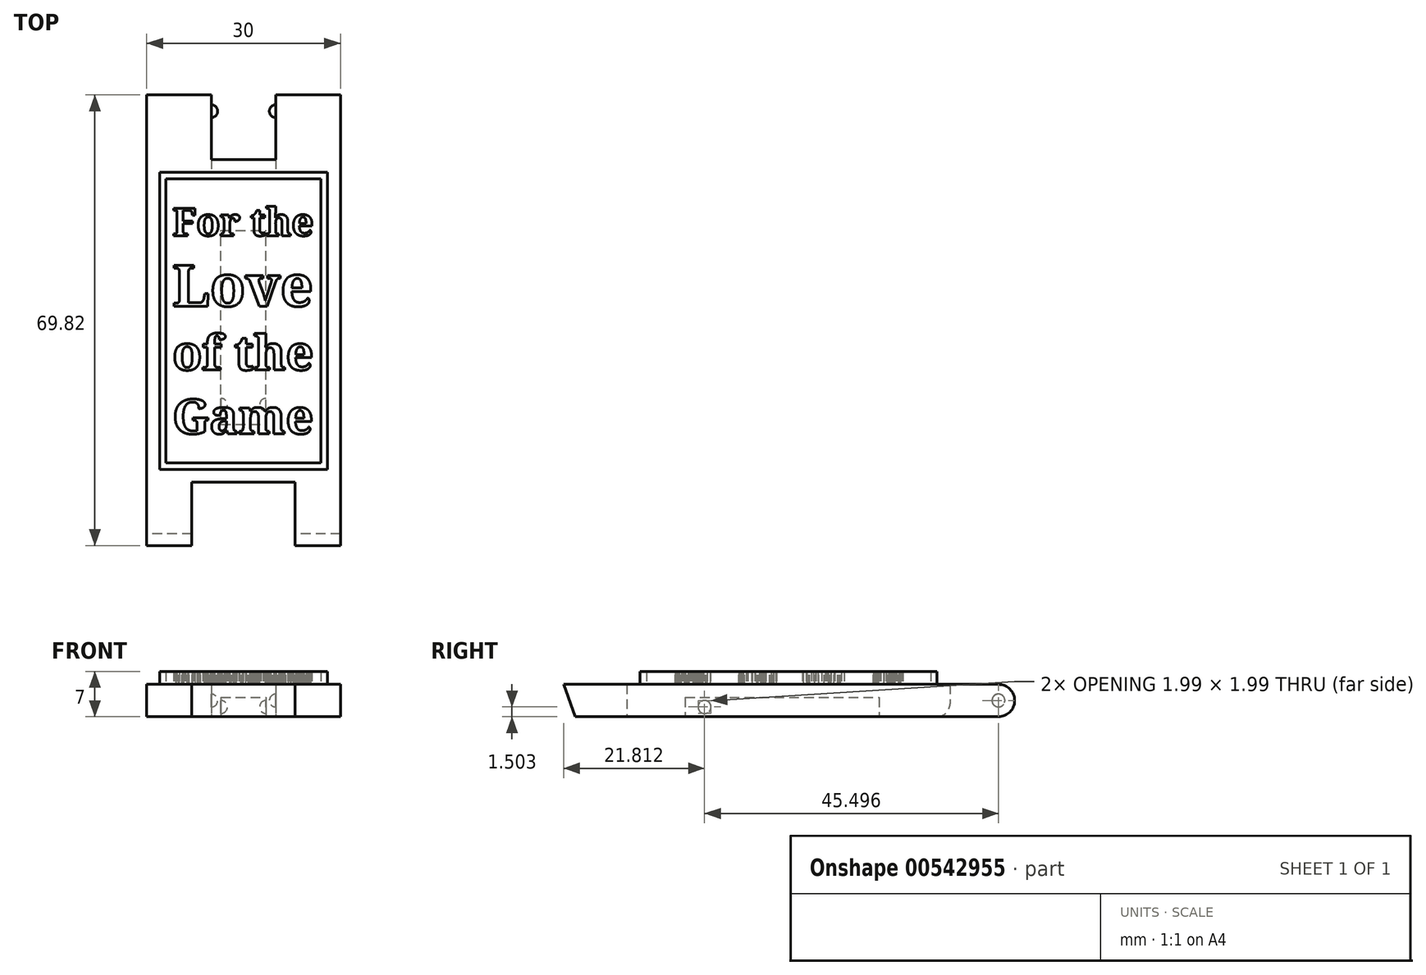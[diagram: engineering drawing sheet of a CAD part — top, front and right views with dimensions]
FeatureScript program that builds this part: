
annotation { "Feature Type Name" : "Feature", "Feature Type Description" : "" }
export const myFeature = defineFeature(function(context is Context, id is Id, definition is map)
    precondition{}
    {
        {
            var Q0;
            Q0=qCreatedBy(makeId("Top.planeOp"),FACE);
            var sketch = newSketch(context, id + "F0", { "sketchPlane" : qUnion([Q0])});
            skLineSegment(sketch, "E0.bottom", {"start": v(-23.2, 19.17) * mm, "end": v(6.8, 19.17) * mm});
            skLineSegment(sketch, "E0.top", {"start": v(-23.2, -30.83) * mm, "end": v(6.8, -30.83) * mm});
            skLineSegment(sketch, "E0.left", {"start": v(-23.2, 19.17) * mm, "end": v(-23.2, -30.83) * mm});
            skLineSegment(sketch, "E0.right", {"start": v(6.8, 19.17) * mm, "end": v(6.8, -30.83) * mm});
            skLineSegment(sketch, "E1.bottom", {"start": v(-23.2, 19.17) * mm, "end": v(-13.2, 19.17) * mm});
            skLineSegment(sketch, "E1.top", {"start": v(-23.2, 29.17) * mm, "end": v(-13.2, 29.17) * mm});
            skLineSegment(sketch, "E1.left", {"start": v(-23.2, 19.17) * mm, "end": v(-23.2, 29.17) * mm});
            skLineSegment(sketch, "E1.right", {"start": v(-13.2, 19.17) * mm, "end": v(-13.2, 29.17) * mm});
            skLineSegment(sketch, "E2.bottom", {"start": v(6.8, 19.17) * mm, "end": v(-3.2, 19.17) * mm});
            skLineSegment(sketch, "E2.top", {"start": v(6.8, 29.17) * mm, "end": v(-3.2, 29.17) * mm});
            skLineSegment(sketch, "E2.left", {"start": v(6.8, 19.17) * mm, "end": v(6.8, 29.17) * mm});
            skLineSegment(sketch, "E2.right", {"start": v(-3.2, 19.17) * mm, "end": v(-3.2, 29.17) * mm});
            skLineSegment(sketch, "E3.bottom", {"start": v(-23.2, -30.83) * mm, "end": v(-16.2, -30.83) * mm});
            skLineSegment(sketch, "E3.top", {"start": v(-23.2, -40.83) * mm, "end": v(-16.2, -40.83) * mm});
            skLineSegment(sketch, "E3.left", {"start": v(-23.2, -30.83) * mm, "end": v(-23.2, -40.83) * mm});
            skLineSegment(sketch, "E3.right", {"start": v(-16.2, -30.83) * mm, "end": v(-16.2, -40.83) * mm});
            skLineSegment(sketch, "E4.bottom", {"start": v(6.8, -30.83) * mm, "end": v(-0.2, -30.83) * mm});
            skLineSegment(sketch, "E4.top", {"start": v(6.8, -40.83) * mm, "end": v(-0.2, -40.83) * mm});
            skLineSegment(sketch, "E4.left", {"start": v(6.8, -30.83) * mm, "end": v(6.8, -40.83) * mm});
            skLineSegment(sketch, "E4.right", {"start": v(-0.2, -30.83) * mm, "end": v(-0.2, -40.83) * mm});
            skSolve(sketch);
        }
        {
            var Q0;
            Q0 = qSketchRegion(id + "F0", true);
            extrude(context, id + "F1", {"entities" : qUnion([Q0]), "depth" : 5 * mm, "offsetDistance" : 25 * mm});
        }
        {
            var Q0;
            Q0=makeQuery(id+"F1.opExtrude","CAP_FACE",FACE,{"disambiguationData":[OSD([sQuery(id+"F0.wireOp",EDGE,"E0.bottom"),sQuery(id+"F0.wireOp",EDGE,"E0.top"),sQuery(id+"F0.wireOp",EDGE,"E0.left"),sQuery(id+"F0.wireOp",EDGE,"E0.right"),sQuery(id+"F0.wireOp",EDGE,"E1.top"),sQuery(id+"F0.wireOp",EDGE,"E1.left"),sQuery(id+"F0.wireOp",EDGE,"E1.right"),sQuery(id+"F0.wireOp",EDGE,"E2.top"),sQuery(id+"F0.wireOp",EDGE,"E2.left"),sQuery(id+"F0.wireOp",EDGE,"E2.right"),sQuery(id+"F0.wireOp",EDGE,"E3.top"),sQuery(id+"F0.wireOp",EDGE,"E3.left"),sQuery(id+"F0.wireOp",EDGE,"E3.right"),sQuery(id+"F0.wireOp",EDGE,"E4.top"),sQuery(id+"F0.wireOp",EDGE,"E4.left"),sQuery(id+"F0.wireOp",EDGE,"E4.right")])],"isStart":false});
            var sketch = newSketch(context, id + "F2", { "sketchPlane" : qUnion([Q0])});
            skLineSegment(sketch, "E5.bottom", {"start": v(-21.2, 17.17) * mm, "end": v(4.8, 17.17) * mm});
            skLineSegment(sketch, "E5.top", {"start": v(-21.2, -28.83) * mm, "end": v(4.8, -28.83) * mm});
            skLineSegment(sketch, "E5.left", {"start": v(-21.2, 17.17) * mm, "end": v(-21.2, -28.83) * mm});
            skLineSegment(sketch, "E5.right", {"start": v(4.8, 17.17) * mm, "end": v(4.8, -28.83) * mm});
            skLineSegment(sketch, "E6.bottom", {"start": v(-20.2, 16.17) * mm, "end": v(3.8, 16.17) * mm});
            skLineSegment(sketch, "E6.top", {"start": v(-20.2, -27.83) * mm, "end": v(3.8, -27.83) * mm});
            skLineSegment(sketch, "E6.left", {"start": v(-20.2, 16.17) * mm, "end": v(-20.2, -27.83) * mm});
            skLineSegment(sketch, "E6.right", {"start": v(3.8, 16.17) * mm, "end": v(3.8, -27.83) * mm});
            skText(sketch, "E7", { "text": "For the", "fontName": "NotoSerif-Bold.ttf"});
            skText(sketch, "E8", { "text": "Love", "fontName": "NotoSerif-Bold.ttf"});
            skText(sketch, "E9", { "text": "of the", "fontName": "NotoSerif-Bold.ttf"});
            skText(sketch, "E10", { "text": "Game", "fontName": "NotoSerif-Bold.ttf"});
            const initialGuessF2  = {"E7": [-0.0192, 0.00736, 1, 0, 0.0043], "E8": [-0.0192, -0.00357, 1, 0, 0.00642], "E9": [-0.0192, -0.01345, 1, 0, 0.00538], "E10": [-0.0192, -0.02333, 1, 0, 0.00537]};
            skSetInitialGuess(sketch, initialGuessF2);
            skSolve(sketch);
        }
        {
            var Q0;
            Q0=makeQuery(id+"F2.imprint","IMPRINT",FACE,{"disambiguationData":[TD([[makeQuery(id+"F2.imprint","IMPRINT",EDGE,{"derivedFrom":sQuery(id+"F2.wireOp",EDGE,"E8.sketch_text.stroke-56")}),-1.0]])]});
            var Q1;
            Q1=makeQuery(id+"F2.imprint","IMPRINT",FACE,{"disambiguationData":[TD([[makeQuery(id+"F2.imprint","IMPRINT",EDGE,{"derivedFrom":sQuery(id+"F2.wireOp",EDGE,"E8.sketch_text.stroke-92")}),-1.0]])]});
            var Q2;
            Q2=makeQuery(id+"F2.imprint","IMPRINT",FACE,{"disambiguationData":[TD([[makeQuery(id+"F2.imprint","IMPRINT",EDGE,{"derivedFrom":sQuery(id+"F2.wireOp",EDGE,"E8.sketch_text.stroke-28")}),-1.0]])]});
            var Q3;
            Q3=makeQuery(id+"F2.imprint","IMPRINT",FACE,{"disambiguationData":[TD([[makeQuery(id+"F2.imprint","IMPRINT",EDGE,{"derivedFrom":sQuery(id+"F2.wireOp",EDGE,"E8.sketch_text.stroke-0")}),-1.0]])]});
            var Q4;
            Q4=makeQuery(id+"F2.imprint","IMPRINT",FACE,{"disambiguationData":[TD([[makeQuery(id+"F2.imprint","IMPRINT",EDGE,{"derivedFrom":sQuery(id+"F2.wireOp",EDGE,"E7.sketch_text.stroke-0")}),-1.0]])]});
            var Q5;
            Q5=makeQuery(id+"F2.imprint","IMPRINT",FACE,{"disambiguationData":[TD([[makeQuery(id+"F2.imprint","IMPRINT",EDGE,{"derivedFrom":sQuery(id+"F2.wireOp",EDGE,"E7.sketch_text.stroke-32")}),-1.0]])]});
            var Q6;
            Q6=makeQuery(id+"F2.imprint","IMPRINT",FACE,{"disambiguationData":[TD([[makeQuery(id+"F2.imprint","IMPRINT",EDGE,{"derivedFrom":sQuery(id+"F2.wireOp",EDGE,"E7.sketch_text.stroke-60")}),-1.0]])]});
            var Q7;
            Q7=makeQuery(id+"F2.imprint","IMPRINT",FACE,{"disambiguationData":[TD([[makeQuery(id+"F2.imprint","IMPRINT",EDGE,{"derivedFrom":sQuery(id+"F2.wireOp",EDGE,"E7.sketch_text.stroke-102")}),-1.0]])]});
            var Q8;
            Q8=makeQuery(id+"F2.imprint","IMPRINT",FACE,{"disambiguationData":[TD([[makeQuery(id+"F2.imprint","IMPRINT",EDGE,{"derivedFrom":sQuery(id+"F2.wireOp",EDGE,"E7.sketch_text.stroke-127")}),-1.0]])]});
            var Q9;
            Q9=makeQuery(id+"F2.imprint","IMPRINT",FACE,{"disambiguationData":[TD([[makeQuery(id+"F2.imprint","IMPRINT",EDGE,{"derivedFrom":sQuery(id+"F2.wireOp",EDGE,"E7.sketch_text.stroke-179")}),-1.0]])]});
            var Q10;
            Q10=makeQuery(id+"F2.imprint","IMPRINT",FACE,{"disambiguationData":[TD([[makeQuery(id+"F2.imprint","IMPRINT",EDGE,{"derivedFrom":sQuery(id+"F2.wireOp",EDGE,"E9.sketch_text.stroke-146")}),-1.0]])]});
            var Q11;
            Q11=makeQuery(id+"F2.imprint","IMPRINT",FACE,{"disambiguationData":[TD([[makeQuery(id+"F2.imprint","IMPRINT",EDGE,{"derivedFrom":sQuery(id+"F2.wireOp",EDGE,"E9.sketch_text.stroke-94")}),-1.0]])]});
            var Q12;
            Q12=makeQuery(id+"F2.imprint","IMPRINT",FACE,{"disambiguationData":[TD([[makeQuery(id+"F2.imprint","IMPRINT",EDGE,{"derivedFrom":sQuery(id+"F2.wireOp",EDGE,"E9.sketch_text.stroke-69")}),-1.0]])]});
            var Q13;
            Q13=makeQuery(id+"F2.imprint","IMPRINT",FACE,{"disambiguationData":[TD([[makeQuery(id+"F2.imprint","IMPRINT",EDGE,{"derivedFrom":sQuery(id+"F2.wireOp",EDGE,"E9.sketch_text.stroke-28")}),-1.0]])]});
            var Q14;
            Q14=makeQuery(id+"F2.imprint","IMPRINT",FACE,{"disambiguationData":[TD([[makeQuery(id+"F2.imprint","IMPRINT",EDGE,{"derivedFrom":sQuery(id+"F2.wireOp",EDGE,"E9.sketch_text.stroke-0")}),-1.0]])]});
            var Q15;
            Q15=makeQuery(id+"F2.imprint","IMPRINT",FACE,{"disambiguationData":[TD([[makeQuery(id+"F2.imprint","IMPRINT",EDGE,{"derivedFrom":sQuery(id+"F2.wireOp",EDGE,"E10.sketch_text.stroke-0")}),-1.0]])]});
            var Q16;
            Q16=makeQuery(id+"F2.imprint","IMPRINT",FACE,{"disambiguationData":[TD([[makeQuery(id+"F2.imprint","IMPRINT",EDGE,{"derivedFrom":sQuery(id+"F2.wireOp",EDGE,"E10.sketch_text.stroke-45")}),-1.0]])]});
            var Q17;
            Q17=makeQuery(id+"F2.imprint","IMPRINT",FACE,{"disambiguationData":[TD([[makeQuery(id+"F2.imprint","IMPRINT",EDGE,{"derivedFrom":sQuery(id+"F2.wireOp",EDGE,"E10.sketch_text.stroke-97")}),-1.0]])]});
            var Q18;
            Q18=makeQuery(id+"F2.imprint","IMPRINT",FACE,{"disambiguationData":[TD([[makeQuery(id+"F2.imprint","IMPRINT",EDGE,{"derivedFrom":sQuery(id+"F2.wireOp",EDGE,"E10.sketch_text.stroke-168")}),-1.0]])]});
            var Q19;
            Q19=makeQuery(id+"F2.imprint","IMPRINT",FACE,{"disambiguationData":[TD([[makeQuery(id+"F2.imprint","IMPRINT",EDGE,{"derivedFrom":sQuery(id+"F2.wireOp",EDGE,"E5.bottom")}),-1.0]])]});
            extrude(context, id + "F3", {"entities" : qUnion([Q0, Q1, Q2, Q3, Q4, Q5, Q6, Q7, Q8, Q9, Q10, Q11, Q12, Q13, Q14, Q15, Q16, Q17, Q18, Q19]), "operationType" : NewBodyOperationType.ADD, "depth" : 2 * mm, "offsetDistance" : 25 * mm});
        }
        {
            var Q0;
            Q0=makeQuery(id+"F1.opExtrude","CAP_EDGE",EDGE,{"disambiguationData":[OSD([sQuery(id+"F0.wireOp",EDGE,"E1.top")])],"isStart":false});
            var Q1;
            Q1=makeQuery(id+"F1.opExtrude","CAP_EDGE",EDGE,{"disambiguationData":[OSD([sQuery(id+"F0.wireOp",EDGE,"E1.top")])],"isStart":true});
            var Q2;
            Q2=makeQuery(id+"F1.opExtrude","CAP_EDGE",EDGE,{"disambiguationData":[OSD([sQuery(id+"F0.wireOp",EDGE,"E2.top")])],"isStart":false});
            var Q3;
            Q3=makeQuery(id+"F1.opExtrude","CAP_EDGE",EDGE,{"disambiguationData":[OSD([sQuery(id+"F0.wireOp",EDGE,"E2.top")])],"isStart":true});
            fillet(context, id + "F4", {"entities" : qUnion([Q0, Q1, Q2, Q3]), "radius" : 2.5 * mm, "tangentPropagation" : true, "allowEdgeOverflow" : false});
        }
        {
            var Q0;
            Q0=makeQuery(id+"F1.opExtrude","SWEPT_FACE",FACE,{"disambiguationData":[OSD([sQuery(id+"F0.wireOp",EDGE,"E2.right")])]});
            var sketch = newSketch(context, id + "F5", { "sketchPlane" : qUnion([Q0])});
            skCircle(sketch, "E11", {"center": v(-26.67, 2.5) * mm, "radius": 1 * mm});
            skLineSegment(sketch, "E12", {"start": v(-26.13, 1.65) * mm, "end": v(-27.2, 3.35) * mm});
            skSolve(sketch);
        }
        {
            var Q0;
            {var subQ0=sQuery(id+"F5.wireOp",EDGE,"E12");Q0=makeQuery(id+"F5.imprint","IMPRINT",FACE,{"disambiguationData":[TD([[makeQuery(id+"F5.imprint","IMPRINT",EDGE,{"derivedFrom":subQ0}),1.0]])]});}
            var Q1;
            Q1=sQuery(id+"F5.wireOp",EDGE,"E12");
            revolve(context, id + "F6", {"operationType" : NewBodyOperationType.ADD, "entities" : qUnion([Q0]), "axis" : qUnion([Q1]), "revolveType" : RevolveType.FULL});
        }
        {
            var Q0;
            Q0=makeQuery(id+"F1.opExtrude","CAP_EDGE",EDGE,{"disambiguationData":[OSD([sQuery(id+"F0.wireOp",EDGE,"E4.top")])],"isStart":true});
            var Q1;
            Q1=makeQuery(id+"F1.opExtrude","CAP_EDGE",EDGE,{"disambiguationData":[OSD([sQuery(id+"F0.wireOp",EDGE,"E3.top")])],"isStart":true});
            chamfer(context, id + "F7", {"entities" : qUnion([Q0, Q1]), "chamferType" : ChamferType.OFFSET_ANGLE, "width" : 2 * mm, "oppositeDirection" : false, "angle" : 70 * degree, "tangentPropagation" : true});
        }
        {
            var Q0;
            Q0=makeQuery(id+"F1.opExtrude","SWEPT_FACE",FACE,{"disambiguationData":[OSD([sQuery(id+"F0.wireOp",EDGE,"E1.right")])]});
            var sketch = newSketch(context, id + "F8", { "sketchPlane" : qUnion([Q0])});
            skCircle(sketch, "E13", {"center": v(26.67, 2.5) * mm, "radius": 1 * mm});
            skLineSegment(sketch, "E14", {"start": v(27.53, 3) * mm, "end": v(25.8, 2) * mm});
            skSolve(sketch);
        }
        {
            var Q0;
            {var subQ0=sQuery(id+"F8.wireOp",EDGE,"E14");Q0=makeQuery(id+"F8.imprint","IMPRINT",FACE,{"disambiguationData":[TD([[makeQuery(id+"F8.imprint","IMPRINT",EDGE,{"derivedFrom":subQ0}),-1.0]])]});}
            var Q1;
            Q1=sQuery(id+"F8.wireOp",EDGE,"E14");
            revolve(context, id + "F9", {"operationType" : NewBodyOperationType.ADD, "entities" : qUnion([Q0]), "axis" : qUnion([Q1]), "revolveType" : RevolveType.FULL, "oppositeDirection" : true});
        }
        {
            var Q0;
            Q0=makeQuery(id+"F1.opExtrude","CAP_EDGE",EDGE,{"disambiguationData":[OSD([sQuery(id+"F0.wireOp",EDGE,"E0.bottom")])],"isStart":true});
            fillet(context, id + "F10", {"entities" : qUnion([Q0]), "radius" : 2 * mm, "tangentPropagation" : true, "allowEdgeOverflow" : false});
        }
        {
            var Q0;
            Q0=makeQuery(id+"F1.opExtrude","CAP_FACE",FACE,{"disambiguationData":[OSD([sQuery(id+"F0.wireOp",EDGE,"E0.bottom"),sQuery(id+"F0.wireOp",EDGE,"E0.top"),sQuery(id+"F0.wireOp",EDGE,"E0.left"),sQuery(id+"F0.wireOp",EDGE,"E0.right"),sQuery(id+"F0.wireOp",EDGE,"E1.top"),sQuery(id+"F0.wireOp",EDGE,"E1.left"),sQuery(id+"F0.wireOp",EDGE,"E1.right"),sQuery(id+"F0.wireOp",EDGE,"E2.top"),sQuery(id+"F0.wireOp",EDGE,"E2.left"),sQuery(id+"F0.wireOp",EDGE,"E2.right"),sQuery(id+"F0.wireOp",EDGE,"E3.top"),sQuery(id+"F0.wireOp",EDGE,"E3.left"),sQuery(id+"F0.wireOp",EDGE,"E3.right"),sQuery(id+"F0.wireOp",EDGE,"E4.top"),sQuery(id+"F0.wireOp",EDGE,"E4.left"),sQuery(id+"F0.wireOp",EDGE,"E4.right")])],"isStart":true});
            var sketch = newSketch(context, id + "F11", { "sketchPlane" : qUnion([Q0])});
            skLineSegment(sketch, "E15.bottom", {"start": v(-11.7, 21.83) * mm, "end": v(-4.7, 21.83) * mm});
            skLineSegment(sketch, "E15.top", {"start": v(-11.7, -8.17) * mm, "end": v(-4.7, -8.17) * mm});
            skLineSegment(sketch, "E15.left", {"start": v(-11.7, 21.83) * mm, "end": v(-11.7, -8.17) * mm});
            skLineSegment(sketch, "E15.right", {"start": v(-4.7, 21.83) * mm, "end": v(-4.7, -8.17) * mm});
            skSolve(sketch);
        }
        {
            var Q0;
            Q0=makeQuery(id+"F11.imprint","IMPRINT",FACE,{"disambiguationData":[TD([[makeQuery(id+"F11.imprint","IMPRINT",EDGE,{"derivedFrom":sQuery(id+"F11.wireOp",EDGE,"E15.bottom")}),-1.0]])]});
            extrude(context, id + "F12", {"entities" : qUnion([Q0]), "operationType" : NewBodyOperationType.REMOVE, "oppositeDirection" : true, "depth" : 3 * mm, "offsetDistance" : 25 * mm});
        }
        {
            var Q0;
            Q0=makeQuery(id+"F12.boolean.opBoolean","COPY",FACE,{"derivedFrom":makeQuery(id+"F12.opExtrude","SWEPT_FACE",FACE,{"disambiguationData":[OSD([sQuery(id+"F11.wireOp",EDGE,"E15.left")])]})});
            var sketch = newSketch(context, id + "F13", { "sketchPlane" : qUnion([Q0])});
            skCircle(sketch, "E16", {"center": v(-18.83, 1.5) * mm, "radius": 1 * mm});
            skPoint(sketch, "E16.centerSnap0", {"position": v(-21.83, 1.5) * mm});
            skLineSegment(sketch, "E17", {"start": v(-18.05, 2.12) * mm, "end": v(-19.62, 0.88) * mm});
            skSolve(sketch);
        }
        {
            var Q0;
            {var subQ0=sQuery(id+"F13.wireOp",EDGE,"E17");Q0=makeQuery(id+"F13.imprint","IMPRINT",FACE,{"disambiguationData":[TD([[makeQuery(id+"F13.imprint","IMPRINT",EDGE,{"derivedFrom":subQ0}),-1.0]])]});}
            var Q1;
            Q1=sQuery(id+"F13.wireOp",EDGE,"E17");
            revolve(context, id + "F14", {"operationType" : NewBodyOperationType.ADD, "entities" : qUnion([Q0]), "axis" : qUnion([Q1]), "revolveType" : RevolveType.FULL});
        }
        {
            var Q0;
            Q0=makeQuery(id+"F12.boolean.opBoolean","COPY",FACE,{"derivedFrom":makeQuery(id+"F12.opExtrude","SWEPT_FACE",FACE,{"disambiguationData":[OSD([sQuery(id+"F11.wireOp",EDGE,"E15.right")])]})});
            var sketch = newSketch(context, id + "F15", { "sketchPlane" : qUnion([Q0])});
            skCircle(sketch, "E18", {"center": v(18.83, 1.5) * mm, "radius": 1 * mm});
            skPoint(sketch, "E18.centerSnap0", {"position": v(21.83, 1.5) * mm});
            skLineSegment(sketch, "E19", {"start": v(19.83, 1.5) * mm, "end": v(17.83, 1.5) * mm});
            skSolve(sketch);
        }
        {
            var Q0;
            {var subQ0=sQuery(id+"F15.wireOp",EDGE,"E19");Q0=makeQuery(id+"F15.imprint","IMPRINT",FACE,{"disambiguationData":[TD([[makeQuery(id+"F15.imprint","IMPRINT",EDGE,{"derivedFrom":subQ0}),1.0]])]});}
            var Q1;
            Q1=sQuery(id+"F15.wireOp",EDGE,"E19");
            revolve(context, id + "F16", {"operationType" : NewBodyOperationType.ADD, "entities" : qUnion([Q0]), "axis" : qUnion([Q1]), "revolveType" : RevolveType.FULL});
        }
    });
